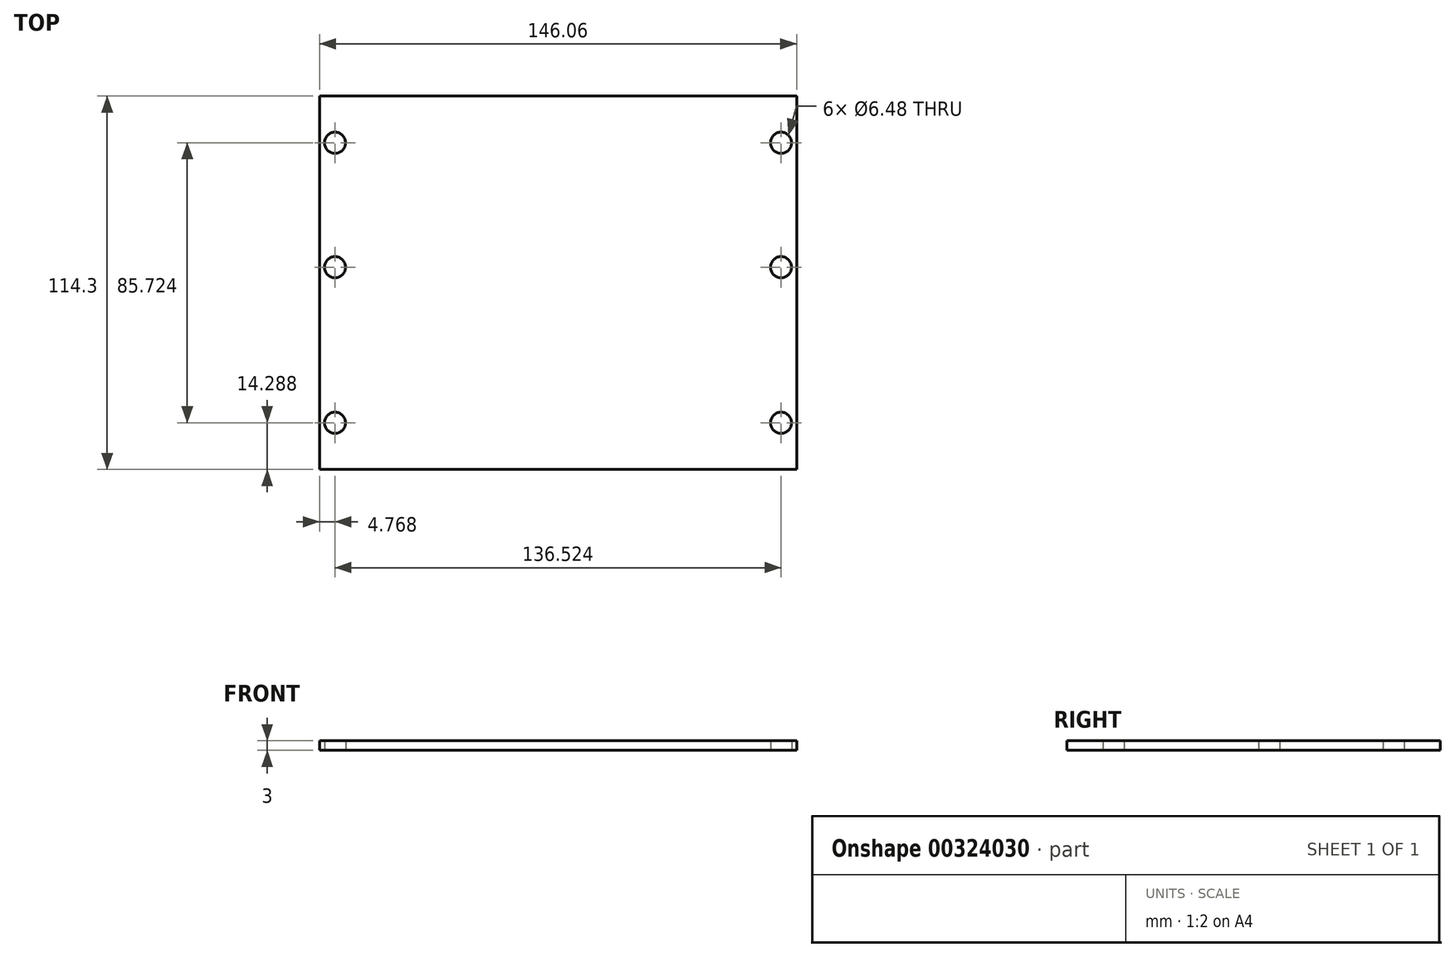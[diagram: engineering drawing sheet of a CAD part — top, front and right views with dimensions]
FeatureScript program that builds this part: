
annotation { "Feature Type Name" : "Feature", "Feature Type Description" : "" }
export const myFeature = defineFeature(function(context is Context, id is Id, definition is map)
    precondition{}
    {
        {
            var Q0;
            Q0=qCreatedBy(makeId("Top.planeOp"),FACE);
            var sketch = newSketch(context, id + "F0", { "sketchPlane" : qUnion([Q0])});
            skArc(sketch, "E0", {"start": v(-68.26, -1.59) * mm, "mid": v(-61.91, 4.76) * mm, "end": v(-68.26, 11.11) * mm});
            skArc(sketch, "E1", {"start": v(68.26, 11.11) * mm, "mid": v(61.91, 4.76) * mm, "end": v(68.26, -1.59) * mm});
            skArc(sketch, "E2", {"start": v(-68.26, 36.51) * mm, "mid": v(-61.91, 42.86) * mm, "end": v(-68.26, 49.21) * mm});
            skArc(sketch, "E3", {"start": v(-68.26, -49.21) * mm, "mid": v(-61.91, -42.86) * mm, "end": v(-68.26, -36.51) * mm});
            skArc(sketch, "E4", {"start": v(68.26, -36.51) * mm, "mid": v(61.91, -42.86) * mm, "end": v(68.26, -49.21) * mm});
            skLineSegment(sketch, "E5", {"start": v(-68.26, 36.51) * mm, "end": v(-72.23, 36.51) * mm});
            skLineSegment(sketch, "E6", {"start": v(-72.23, 11.11) * mm, "end": v(-72.23, 36.51) * mm});
            skLineSegment(sketch, "E7", {"start": v(-68.26, 11.11) * mm, "end": v(-72.23, 11.11) * mm});
            skLineSegment(sketch, "E8", {"start": v(-68.26, -1.59) * mm, "end": v(-72.23, -1.59) * mm});
            skLineSegment(sketch, "E9", {"start": v(-72.23, -36.51) * mm, "end": v(-72.23, -1.59) * mm});
            skLineSegment(sketch, "E10", {"start": v(-68.26, -36.51) * mm, "end": v(-72.23, -36.51) * mm});
            skLineSegment(sketch, "E11", {"start": v(-68.26, -49.21) * mm, "end": v(-72.23, -49.21) * mm});
            skLineSegment(sketch, "E12", {"start": v(-72.23, -56.35) * mm, "end": v(-72.23, -49.21) * mm});
            skLineSegment(sketch, "E13", {"start": v(72.22, -56.35) * mm, "end": v(-72.23, -56.35) * mm});
            skLineSegment(sketch, "E14", {"start": v(72.22, -56.35) * mm, "end": v(72.22, -49.21) * mm});
            skLineSegment(sketch, "E15", {"start": v(68.26, -49.21) * mm, "end": v(72.22, -49.21) * mm});
            skLineSegment(sketch, "E16", {"start": v(68.26, -36.51) * mm, "end": v(72.22, -36.51) * mm});
            skLineSegment(sketch, "E17", {"start": v(72.22, -36.51) * mm, "end": v(72.22, -1.59) * mm});
            skLineSegment(sketch, "E18", {"start": v(68.26, -1.59) * mm, "end": v(72.22, -1.59) * mm});
            skLineSegment(sketch, "E19", {"start": v(68.26, 11.11) * mm, "end": v(72.22, 11.11) * mm});
            skLineSegment(sketch, "E20", {"start": v(72.22, 11.11) * mm, "end": v(72.22, 36.51) * mm});
            skLineSegment(sketch, "E21", {"start": v(68.26, 36.51) * mm, "end": v(72.22, 36.51) * mm});
            skArc(sketch, "E22", {"start": v(68.26, 49.21) * mm, "mid": v(61.91, 42.86) * mm, "end": v(68.26, 36.51) * mm});
            skLineSegment(sketch, "E23", {"start": v(68.26, 49.21) * mm, "end": v(72.22, 49.21) * mm});
            skLineSegment(sketch, "E24", {"start": v(72.22, 49.21) * mm, "end": v(72.22, 56.35) * mm});
            skLineSegment(sketch, "E25", {"start": v(72.22, 56.35) * mm, "end": v(-72.23, 56.35) * mm});
            skLineSegment(sketch, "E26", {"start": v(-72.23, 49.21) * mm, "end": v(-72.23, 56.35) * mm});
            skLineSegment(sketch, "E27", {"start": v(-68.26, 49.21) * mm, "end": v(-72.23, 49.21) * mm});
            skCircle(sketch, "E28", {"center": v(-68.26, -42.86) * mm, "radius": 3.24 * mm});
            skCircle(sketch, "E29", {"center": v(68.26, 42.86) * mm, "radius": 3.24 * mm});
            skCircle(sketch, "E30", {"center": v(-68.26, 4.76) * mm, "radius": 3.24 * mm});
            skCircle(sketch, "E31", {"center": v(68.26, 4.76) * mm, "radius": 3.24 * mm});
            skLineSegment(sketch, "E32", {"start": v(73.03, -57.15) * mm, "end": v(73.03, 57.15) * mm});
            skCircle(sketch, "E33", {"center": v(-68.26, 42.86) * mm, "radius": 3.24 * mm});
            skLineSegment(sketch, "E34", {"start": v(-73.03, -57.15) * mm, "end": v(-73.03, 57.15) * mm});
            skLineSegment(sketch, "E35", {"start": v(73.03, 57.15) * mm, "end": v(-73.03, 57.15) * mm});
            skLineSegment(sketch, "E36", {"start": v(73.03, -57.15) * mm, "end": v(-73.03, -57.15) * mm});
            skCircle(sketch, "E37", {"center": v(68.26, -42.86) * mm, "radius": 3.24 * mm});
            skSolve(sketch);
        }
        {
            var Q0;
            Q0 = qSketchRegion(id + "F0", true);
            var Q1;
            Q1=makeQuery(id+"F0.imprint","IMPRINT",FACE,{"disambiguationData":[TD([[makeQuery(id+"F0.imprint","IMPRINT",EDGE,{"derivedFrom":sQuery(id+"F0.wireOp",EDGE,"E5")}),1.0]])]});
            extrude(context, id + "F1", {"entities" : qUnion([Q0, Q1]), "depth" : 3 * mm});
        }
    });
